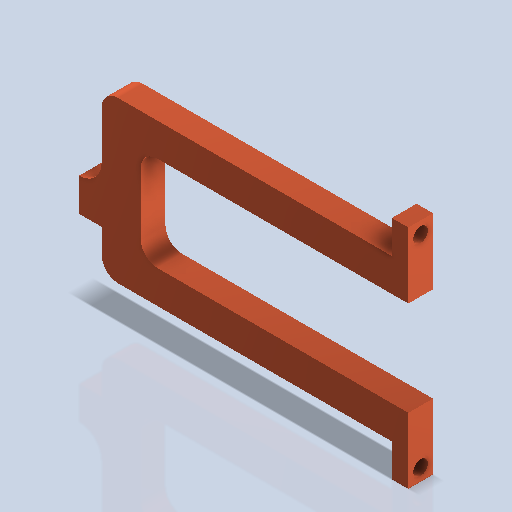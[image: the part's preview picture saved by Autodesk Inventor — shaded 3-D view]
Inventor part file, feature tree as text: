
AUTODESK INVENTOR PART (.ipt)
format: ipt  version: 2024.2 (Build 282272000, 272)  size: 291,840 bytes
history: native  units: mm
features: sketch x3, hole x2, extrude x1
ambient origin geometry x8: Origin, YZ Plane, XZ Plane, XY Plane, X Axis, Y Axis, Z Axis, Center Point
bodies: Volumenkörper1 (feature_tree)
feature tree (6):
  extrude  "Extrusion1"  Depth=57.5mm
  hole  "Bohrung1"  [1 undecoded]
  hole  "Bohrung2"  [1 undecoded]
  sketch  "Skizze1"  dims[d3=57.5mm d4=57.5mm]
  sketch  "Skizze2"  dims[d7=20.0mm d8=20.0mm]
  sketch  "Skizze3"  dims[d9=47.5mm d10=27.5mm d11=40.0mm d12=47.5mm d13=27.5mm d14=27.5mm d18=97.5mm d19=97.5mm d20=20.0mm d22=40.0mm d24=305.0mm d25=30.0mm d26=0.0mm d27=15.29367mm d28=36.0mm d29=4.0mm d30=2.0mm d31=90.0deg d32=45.0mm d33=0.0mm d34=24.0mm d36=18.0mm d37=20.0mm d38=4.0mm d39=2.0mm d40=90.0deg d41=37.5mm d42=0.0mm d43=15.0mm d44=15.0mm d45=40.0mm d46=40.0mm d47=40.0mm]
note: 2 required parameter values undecoded (feature->parameter linkage not recoverable at this tier; creation-order binding heuristic only, values carry confidence <= 0.55)
